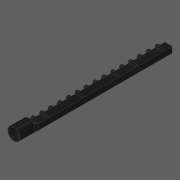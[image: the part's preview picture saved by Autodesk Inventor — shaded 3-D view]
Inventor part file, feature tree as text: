
AUTODESK INVENTOR PART (.ipt)
format: ipt  version: 2020 (Build 240168000, 168)  size: 342,528 bytes
history: native  units: in
note: dims shown in document units (in); Inventor stores cm internally (conversion verified against a paired STEP export)
features: other x8, extrude x4, loft x2, pattern_linear x1, projected_geometry x1
ambient origin geometry x8: Origin, YZ Plane, XZ Plane, XY Plane, X Axis, Y Axis, Z Axis, Center Point
bodies: Solid1 (feature_tree)
feature tree (16):
  other  "Box Sketch"
  extrude  "Box"  Depth=0.063in
  other  "Fitting Plane"
  other  "Fitting"
  extrude  "Fitting Entrance"  Depth=0.0315in
  pattern_linear  "Channel Repetition"  Spacing1=0.0315in  [1 undecoded]
  extrude  "Tabs"  Depth=0.4882in TaperAngle=0.0deg
  other  "Mouthpiece Plane"
  other  "Mouthpiece Sketch"
  loft  "Mouthpiece Loft (outer)"
  loft  "Mouthpiece Loft (inner)"
  extrude  "Extrusion5"  Depth=0.0197in
  other  "Fitting Sketch"
  other  "Fitting Entrance Sketch"
  projected_geometry  "Projected Loop1"
  other  "Tab Sketch"
note: 1 required parameter value undecoded (feature->parameter linkage not recoverable at this tier; creation-order binding heuristic only, values carry confidence <= 0.55)
